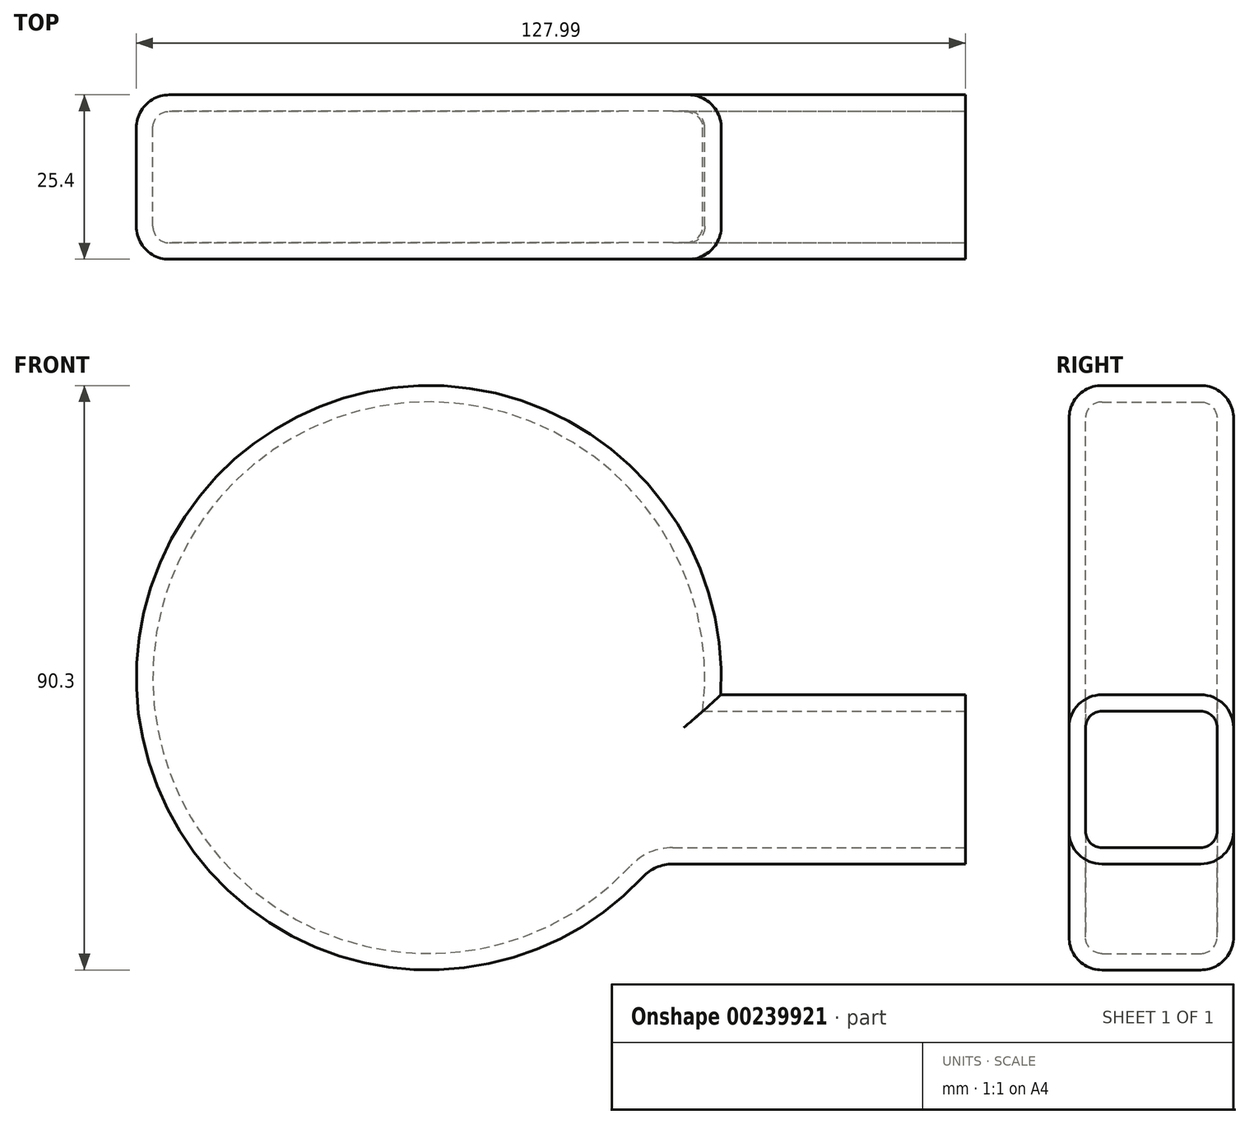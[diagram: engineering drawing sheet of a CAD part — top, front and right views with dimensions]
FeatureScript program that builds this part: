
annotation { "Feature Type Name" : "Feature", "Feature Type Description" : "" }
export const myFeature = defineFeature(function(context is Context, id is Id, definition is map)
    precondition{}
    {
        {
            var Q0;
            Q0=qCreatedBy(makeId("Front.planeOp"),FACE);
            var sketch = newSketch(context, id + "F0", { "sketchPlane" : qUnion([Q0])});
            skArc(sketch, "E0", {"start": v(45.08, -2.63) * mm, "mid": v(-41.5, 17.77) * mm, "end": v(33.02, -30.8) * mm});
            skLineSegment(sketch, "E1.bottom", {"start": v(45.08, -2.63) * mm, "end": v(82.84, -2.63) * mm});
            skLineSegment(sketch, "E1.top", {"start": v(37.66, -28.78) * mm, "end": v(82.84, -28.78) * mm});
            skLineSegment(sketch, "E1.right", {"start": v(82.84, -2.63) * mm, "end": v(82.84, -28.78) * mm});
            skPoint(sketch, "E2.visualSharp", {"position": v(34.79, -28.78) * mm});
            skArc(sketch, "E2.filletArc", {"start": v(37.66, -28.78) * mm, "mid": v(35.13, -29.3) * mm, "end": v(33.02, -30.8) * mm});
            skSolve(sketch);
        }
        {
            var Q0;
            Q0 = qSketchRegion(id + "F0", true);
            extrude(context, id + "F1", {"entities" : qUnion([Q0]), "depth" : 25.4 * mm});
        }
        {
            var Q0;
            Q0=makeQuery(id+"F1.opExtrude","CAP_EDGE",EDGE,{"disambiguationData":[OSD([sQuery(id+"F0.wireOp",EDGE,"E1.top")])],"isStart":false});
            var Q1;
            Q1=makeQuery(id+"F1.opExtrude","CAP_EDGE",EDGE,{"disambiguationData":[OSD([sQuery(id+"F0.wireOp",EDGE,"E1.bottom")])],"isStart":false});
            var Q2;
            Q2=makeQuery(id+"F1.opExtrude","CAP_EDGE",EDGE,{"disambiguationData":[OSD([sQuery(id+"F0.wireOp",EDGE,"E0")])],"isStart":false});
            var Q3;
            Q3=makeQuery(id+"F1.opExtrude","CAP_EDGE",EDGE,{"disambiguationData":[OSD([sQuery(id+"F0.wireOp",EDGE,"E1.top")])],"isStart":true});
            var Q4;
            Q4=makeQuery(id+"F1.opExtrude","CAP_EDGE",EDGE,{"disambiguationData":[OSD([sQuery(id+"F0.wireOp",EDGE,"E1.bottom")])],"isStart":true});
            var Q5;
            Q5=makeQuery(id+"F1.opExtrude","CAP_EDGE",EDGE,{"disambiguationData":[OSD([sQuery(id+"F0.wireOp",EDGE,"E0")])],"isStart":true});
            fillet(context, id + "F2", {"entities" : qUnion([Q0, Q1, Q2, Q3, Q4, Q5]), "radius" : 5.08 * mm, "tangentPropagation" : true, "allowEdgeOverflow" : false});
        }
        {
            var Q0;
            Q0=makeQuery(id+"F1.opExtrude","SWEPT_FACE",FACE,{"disambiguationData":[OSD([sQuery(id+"F0.wireOp",EDGE,"E1.right")])]});
            shell(context, id + "F3", {"entities" : qUnion([Q0]), "thickness" : 2.54 * mm});
        }
        {
            var Q0;
            Q0=qCreatedBy(makeId("Right.planeOp"),FACE);
            var sketch = newSketch(context, id + "F4", { "sketchPlane" : qUnion([Q0])});
            skLineSegment(sketch, "E3.bottom", {"start": v(-20.11, -23.46) * mm, "end": v(-5.25, -23.46) * mm});
            skLineSegment(sketch, "E3.top", {"start": v(-20.11, -7.72) * mm, "end": v(-5.25, -7.72) * mm});
            skLineSegment(sketch, "E3.left", {"start": v(-20.11, -23.46) * mm, "end": v(-20.11, -7.72) * mm});
            skLineSegment(sketch, "E3.right", {"start": v(-5.25, -23.46) * mm, "end": v(-5.25, -7.72) * mm});
            skSolve(sketch);
        }
        {
            var Q0;
            Q0=makeQuery(id+"F4.imprint","IMPRINT",FACE,{"disambiguationData":[TD([[makeQuery(id+"F4.imprint","IMPRINT",EDGE,{"derivedFrom":sQuery(id+"F4.wireOp",EDGE,"E3.bottom")}),1.0]])]});
            extrude(context, id + "F5", {"entities" : qUnion([Q0]), "operationType" : NewBodyOperationType.REMOVE, "oppositeDirection" : true, "depth" : 25.4 * mm});
        }
        {
            var Q0;
            Q0=qCreatedBy(makeId("Right.planeOp"),FACE);
            var sketch = newSketch(context, id + "F6", { "sketchPlane" : qUnion([Q0])});
            skLineSegment(sketch, "E4", {"start": v(-20.7, -5.98) * mm, "end": v(-5.83, -5.98) * mm});
            skLineSegment(sketch, "E5", {"start": v(-5.25, -24.34) * mm, "end": v(-20.99, -24.34) * mm});
            skLineSegment(sketch, "E6", {"start": v(-20.99, -24.34) * mm, "end": v(-20.7, -5.98) * mm});
            skLineSegment(sketch, "E7", {"start": v(-5.83, -5.98) * mm, "end": v(-5.25, -24.34) * mm});
            skSolve(sketch);
        }
        {
            var Q0;
            Q0=makeQuery(id+"F6.imprint","IMPRINT",FACE,{"disambiguationData":[TD([[makeQuery(id+"F6.imprint","IMPRINT",EDGE,{"derivedFrom":sQuery(id+"F6.wireOp",EDGE,"E4")}),-1.0]])]});
            extrude(context, id + "F7", {"entities" : qUnion([Q0]), "operationType" : NewBodyOperationType.REMOVE, "depth" : 175 * mm});
        }
    });
